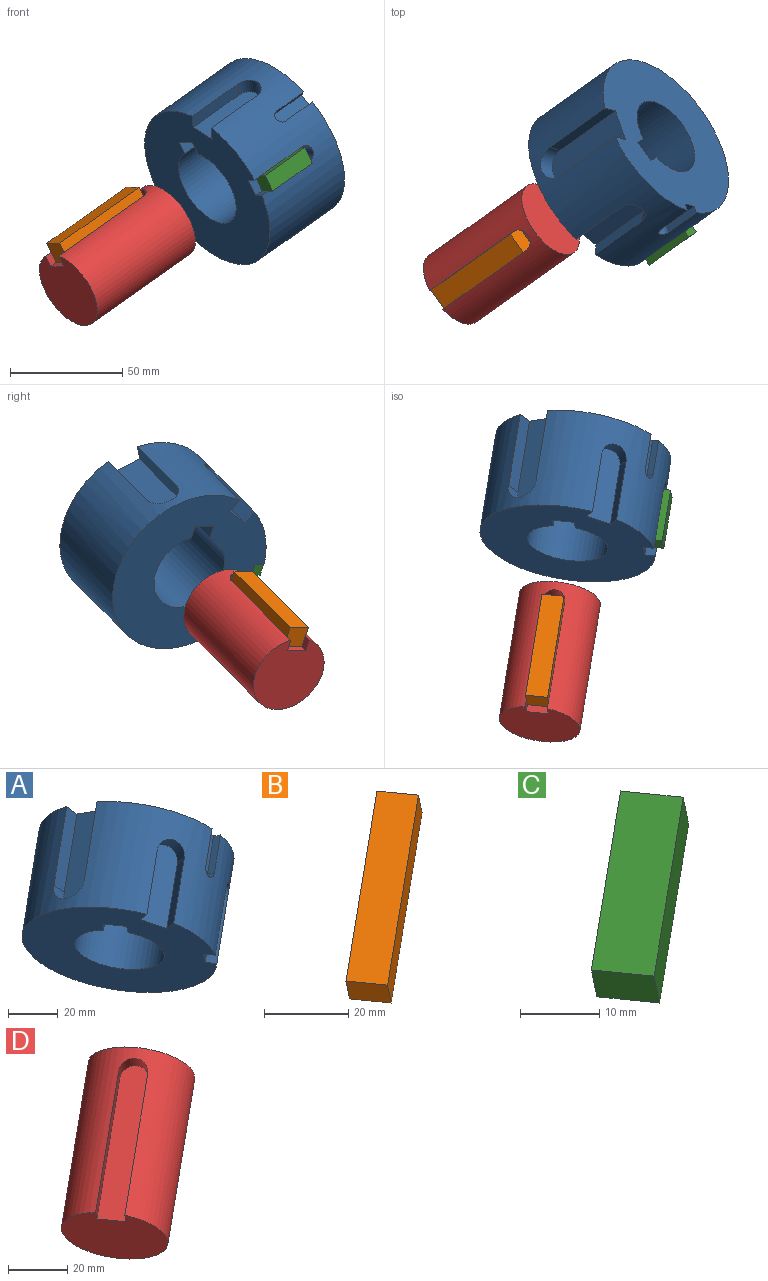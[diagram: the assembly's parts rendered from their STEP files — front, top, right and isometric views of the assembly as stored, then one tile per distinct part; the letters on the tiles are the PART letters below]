
ASSEMBLY  parts=4 mates=3
PART A: 23 faces, bbox 89.1x92x92 mm
  f0: cylinder r=39.53mm len=91.96mm, axis (0.71,0.5,0.5), area 10267.8mm2, adj f1,f2,f8,f9,f10,f12,f13,f14
  f1: plane 68.46x68.46mm, normal (0.71,0.5,0.5), area 3675.6mm2, adj f0,f3,f4,f5,f6,f11,f12,f13
  f2: plane 68.46x68.46mm, normal (-0.71,-0.5,-0.5), area 3691.2mm2, adj f0,f3,f4,f5,f6,f7,f8,f9
  f3: cylinder r=18.21mm len=58.98mm, axis (0.71,0.5,0.5), area 4900mm2, adj f1,f2,f5,f6
  f4: plane 39.01x31.67mm, normal (0.41,0.29,-0.87), area 470mm2, adj f1,f2,f5,f6
  f5: plane 35.64x28.61mm, normal (0.58,-0.82,0), area 277.3mm2, adj f1,f2,f3,f4
  f6: plane 35.64x28.61mm, normal (-0.58,0.82,0), area 277.3mm2, adj f1,f2,f3,f4
  f7: plane 26.11x22.46mm, normal (0.58,-0.82,0), area 265.1mm2, adj f2,f8,f9,f10
  f8: plane 23.98x18.92mm, normal (0.41,0.29,-0.87), area 143.9mm2, adj f0,f2,f7,f10
  f9: plane 23.98x18.92mm, normal (-0.41,-0.29,0.87), area 143.9mm2, adj f0,f2,f7,f10
  f10: cylinder r=4mm len=7.79mm, axis (-0.58,0.82,0), area 61.6mm2, adj f0,f7,f8,f9
  f11: plane 32.72x31.29mm, normal (-0.64,0.16,0.75), area 613.4mm2, adj f1,f12,f13,f14
  f12: plane 29.43x22.96mm, normal (-0.3,0.85,-0.43), area 254.9mm2, adj f0,f1,f11,f14
  f13: plane 29.43x22.96mm, normal (0.3,-0.85,0.43), area 254.9mm2, adj f0,f1,f11,f14
  f14: cylinder r=7.5mm len=15.06mm, axis (0.64,-0.16,-0.75), area 180.1mm2, adj f0,f11,f12,f13
  f15: plane 20.93x19.41mm, normal (0.7,-0.56,-0.43), area 189.7mm2, adj f0,f2,f17,f18
  f16: plane 20.93x19.41mm, normal (-0.7,0.56,0.43), area 189.7mm2, adj f0,f2,f17,f18
  f17: plane 30.72x22.39mm, normal (-0.06,-0.66,0.75), area 404.5mm2, adj f2,f15,f16,f18
  f18: cylinder r=6mm len=12.5mm, axis (0.06,0.66,-0.75), area 127.6mm2, adj f0,f15,f16,f17
  f19: plane 16.81x13.45mm, normal (0.3,-0.85,0.43), area 116.1mm2, adj f1,f20,f21,f22
  f20: plane 13.02x11.38mm, normal (-0.64,0.16,0.75), area 57.6mm2, adj f0,f1,f19,f22
  f21: plane 13.02x11.38mm, normal (0.64,-0.16,-0.75), area 57.6mm2, adj f0,f1,f19,f22
  f22: cylinder r=3mm len=6.47mm, axis (-0.3,0.85,-0.43), area 32.4mm2, adj f0,f19,f20,f21
PART B: 6 faces, bbox 45.2x36.1x33.7 mm
  f0: plane 41.13x33.17mm, normal (0.41,0.29,-0.87), area 500mm2, adj f1,f3,f4,f5
  f1: plane 39.44x33.66mm, normal (-0.58,0.82,0), area 500mm2, adj f0,f2,f4,f5
  f2: plane 41.13x33.17mm, normal (-0.41,-0.29,0.87), area 500mm2, adj f1,f3,f4,f5
  f3: plane 39.44x33.66mm, normal (0.58,-0.82,0), area 500mm2, adj f0,f2,f4,f5
  f4: plane 11.05x9.86mm, normal (0.71,0.5,0.5), area 100mm2, adj f0,f1,f2,f3
  f5: plane 11.05x9.86mm, normal (-0.71,-0.5,-0.5), area 100mm2, adj f0,f1,f2,f3
PART C: 6 faces, bbox 25.6x21.3x19.4 mm
  f0: plane 20.94x19.43mm, normal (-0.58,0.82,0), area 200mm2, adj f1,f3,f4,f5
  f1: plane 22.3x19.03mm, normal (-0.41,-0.29,0.87), area 200mm2, adj f0,f2,f4,f5
  f2: plane 20.94x19.43mm, normal (0.58,-0.82,0), area 200mm2, adj f1,f3,f4,f5
  f3: plane 22.3x19.03mm, normal (0.41,0.29,-0.87), area 200mm2, adj f0,f2,f4,f5
  f4: plane 8.84x7.88mm, normal (0.71,0.5,0.5), area 64mm2, adj f0,f1,f2,f3
  f5: plane 8.84x7.88mm, normal (-0.71,-0.5,-0.5), area 64mm2, adj f0,f1,f2,f3
PART D: 7 faces, bbox 69.6x62.5x62.5 mm
  f0: cylinder r=18.21mm len=69.59mm, axis (0.71,0.5,0.5), area 6515.4mm2, adj f1,f2,f3,f4,f6
  f1: plane 31.53x30.93mm, normal (-0.71,-0.5,-0.5), area 983.5mm2, adj f0,f3,f4,f5
  f2: plane 31.53x31.53mm, normal (0.71,0.5,0.5), area 1041.2mm2, adj f0
  f3: plane 39.64x31.09mm, normal (0.58,-0.82,0), area 280.9mm2, adj f0,f1,f5,f6
  f4: plane 39.64x31.09mm, normal (-0.58,0.82,0), area 280.9mm2, adj f0,f1,f5,f6
  f5: plane 44.93x35.37mm, normal (-0.41,-0.29,0.87), area 569.3mm2, adj f1,f3,f4,f6
  f6: cylinder r=5mm len=10.6mm, axis (0.41,0.29,-0.87), area 88.8mm2, adj f0,f3,f4,f5
PLACE A t=(33.23,23.5,23.5)mm fixed
PLACE B t=(-17.83,-13.07,-14.36)mm
PLACE C t=(32.59,23.04,23.04)mm
PLACE D t=(-18.17,-13.31,-14.6)mm
MATE fastened D.f5 <-> B.f0  axis (-0.41,-0.29,0.87) through (-46.85,-33.59,-20.79)mm
MATE fastened A.f7 <-> C.f0  axis (0.58,-0.82,0) through (31.66,-19.9,8.29)mm
MATE slider D.f0 <-> A.f1  axis (0.71,0.5,0.5) through (-18.17,-13.31,-14.6)mm
